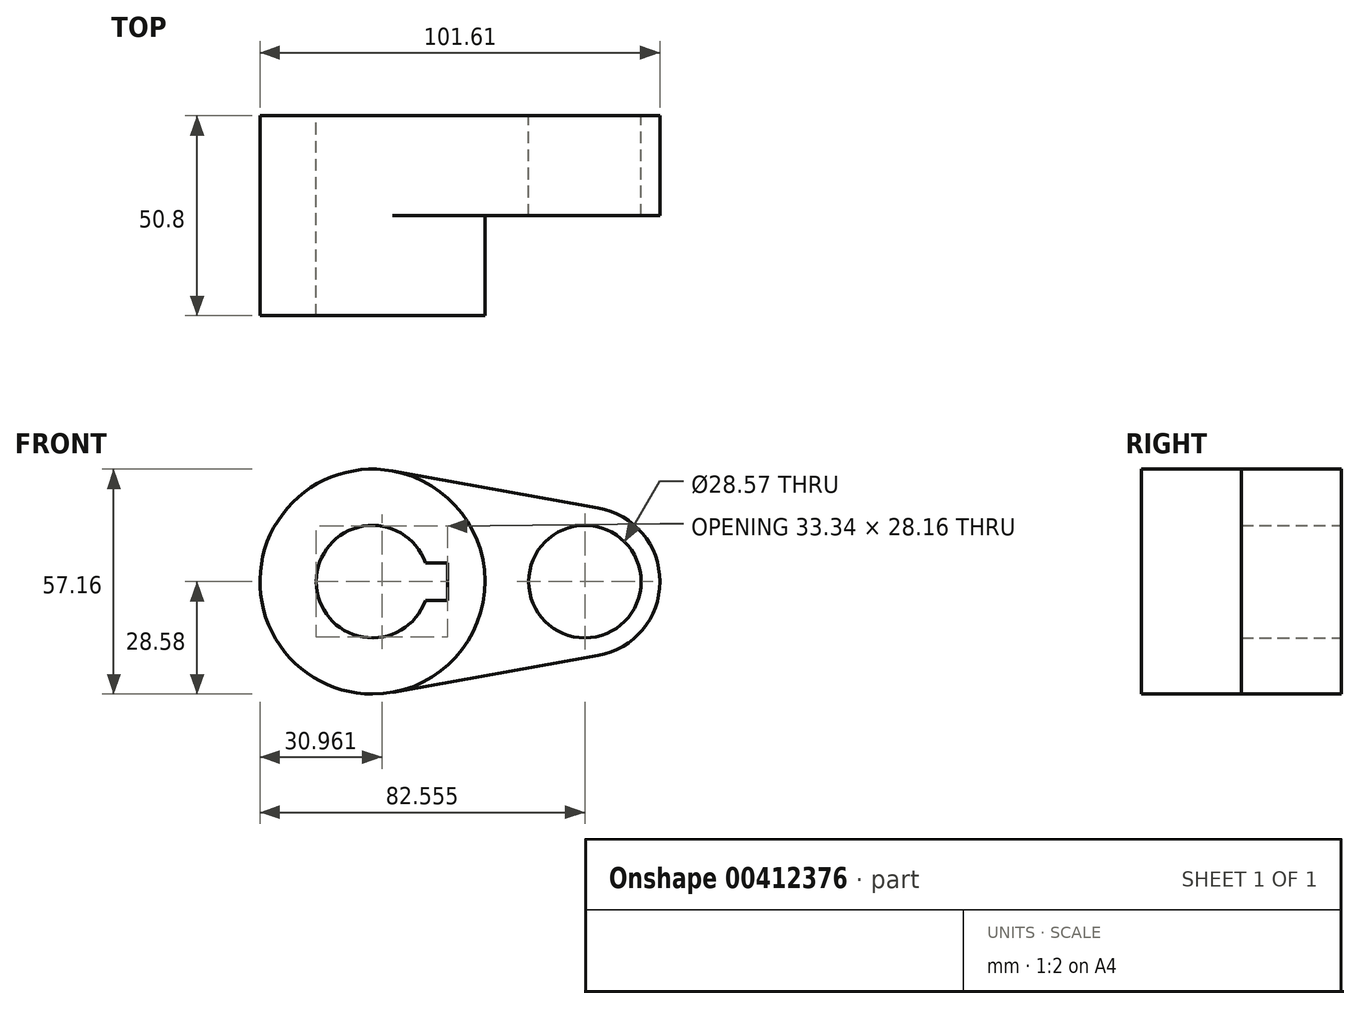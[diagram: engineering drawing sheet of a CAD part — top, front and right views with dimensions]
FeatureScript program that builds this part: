
annotation { "Feature Type Name" : "Feature", "Feature Type Description" : "" }
export const myFeature = defineFeature(function(context is Context, id is Id, definition is map)
    precondition{}
    {
        {
            var Q0;
            Q0=qCreatedBy(makeId("Front.planeOp"),FACE);
            var sketch = newSketch(context, id + "F0", { "sketchPlane" : qUnion([Q0])});
            skCircle(sketch, "E0", {"center": v(0, 0) * mm, "radius": 28.58 * mm});
            skCircle(sketch, "E1", {"center": v(53.97, 0) * mm, "radius": 19.05 * mm});
            skLineSegment(sketch, "E2", {"start": v(5.04, 28.13) * mm, "end": v(57.34, 18.75) * mm});
            skLineSegment(sketch, "E3", {"start": v(5.04, -28.13) * mm, "end": v(57.34, -18.75) * mm});
            skCircle(sketch, "E4", {"center": v(0, 0) * mm, "radius": 14.29 * mm});
            skCircle(sketch, "E5", {"center": v(53.97, 0) * mm, "radius": 14.29 * mm});
            skLineSegment(sketch, "E6.bottom", {"start": v(19.05, 4.76) * mm, "end": v(-19.05, 4.76) * mm});
            skLineSegment(sketch, "E6.top", {"start": v(19.05, -4.76) * mm, "end": v(-19.05, -4.76) * mm});
            skLineSegment(sketch, "E6.left", {"start": v(19.05, 4.76) * mm, "end": v(19.05, -4.76) * mm});
            skLineSegment(sketch, "E6.right", {"start": v(-19.05, 4.76) * mm, "end": v(-19.05, -4.76) * mm});
            skSolve(sketch);
        }
        {
            var Q0;
            Q0=makeQuery(id+"F0.imprint","IMPRINT",FACE,{"disambiguationData":[TD([[makeQuery(id+"F0.imprint","IMPRINT",EDGE,{"derivedFrom":sQuery(id+"F0.wireOp",EDGE,"E5")}),-1.0]])]});
            var Q1;
            {var subQ7=sQuery(id+"F0.wireOp",EDGE,"E6.left");Q1=makeQuery(id+"F0.imprint","IMPRINT",FACE,{"disambiguationData":[TD([[makeQuery(id+"F0.imprint","IMPRINT",EDGE,{"derivedFrom":subQ7}),1.0]])]});}
            var Q2;
            {var subQ5=sQuery(id+"F0.wireOp",EDGE,"E6.right");Q2=makeQuery(id+"F0.imprint","IMPRINT",FACE,{"disambiguationData":[TD([[makeQuery(id+"F0.imprint","IMPRINT",EDGE,{"derivedFrom":subQ5}),1.0]])]});}
            var Q3;
            {var subQ0=sQuery(id+"F0.wireOp",EDGE,"E2");Q3=makeQuery(id+"F0.imprint","IMPRINT",FACE,{"disambiguationData":[TD([[makeQuery(id+"F0.imprint","IMPRINT",EDGE,{"derivedFrom":subQ0}),-1.0]])]});}
            extrude(context, id + "F1", {"entities" : qUnion([Q0, Q1, Q2, Q3]), "depth" : 25.4 * mm});
        }
        {
            var Q0;
            {var subQ7=sQuery(id+"F0.wireOp",EDGE,"E6.left");Q0=makeQuery(id+"F0.imprint","IMPRINT",FACE,{"disambiguationData":[TD([[makeQuery(id+"F0.imprint","IMPRINT",EDGE,{"derivedFrom":subQ7}),1.0]])]});}
            var Q1;
            {var subQ5=sQuery(id+"F0.wireOp",EDGE,"E6.right");Q1=makeQuery(id+"F0.imprint","IMPRINT",FACE,{"disambiguationData":[TD([[makeQuery(id+"F0.imprint","IMPRINT",EDGE,{"derivedFrom":subQ5}),1.0]])]});}
            extrude(context, id + "F2", {"entities" : qUnion([Q0, Q1]), "operationType" : NewBodyOperationType.ADD, "depth" : 50.8 * mm});
        }
    });
